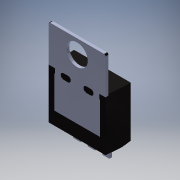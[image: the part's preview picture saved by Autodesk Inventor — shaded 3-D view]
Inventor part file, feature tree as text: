
AUTODESK INVENTOR PART (.ipt)
format: ipt  version: 2018 (Build 220112000, 112)  size: 584,192 bytes
history: native  units: in
note: dims shown in document units (in); Inventor stores cm internally (conversion verified against a paired STEP export)
features: other x10, fillet x3, extrude x2, sketch x2
ambient origin geometry x8: Origin, YZ Plane, XZ Plane, XY Plane, X Axis, Y Axis, Z Axis, Center Point
bodies: Solid1 (feature_tree), Solid2 (feature_tree), Solid3 (feature_tree), Solid4 (feature_tree), Solid5 (feature_tree), Solid6 (feature_tree), Solid7 (feature_tree), Solid8 (feature_tree), Solid9 (feature_tree), Solid10 (feature_tree), Solid11 (feature_tree), Solid12 (feature_tree), Solid13 (feature_tree)
feature tree (17):
  extrude  "Extrusion1"  Depth=0.3937in TaperAngle=0.0deg
  extrude  "Extrusion2"  [1 undecoded]
  sketch  "Sketch1"  dims[d0=0.3937in d1=0.0in d2=0.3937in d3=0.0in]
  sketch  "Sketch2"
  fillet  "Fillet1"  [1 undecoded]
  fillet  "Fillet2"  [1 undecoded]
  fillet  "Fillet9"  [1 undecoded]
  other  "Boss-Extrude9[1]"
  other  "Boss-Extrude9[2]"
  other  "Boss-Extrude9[3]"
  other  "Boss-Extrude9[4]"
  other  "Boss-Extrude9[5]"
  other  "Boss-Extrude9[6]"
  other  "Boss-Extrude9[7]"
  other  "Boss-Extrude9[8]"
  other  "Boss-Extrude9[9]"
  other  "Boss-Extrude9[10]"
note: 4 required parameter values undecoded (feature->parameter linkage not recoverable at this tier; creation-order binding heuristic only, values carry confidence <= 0.55)
